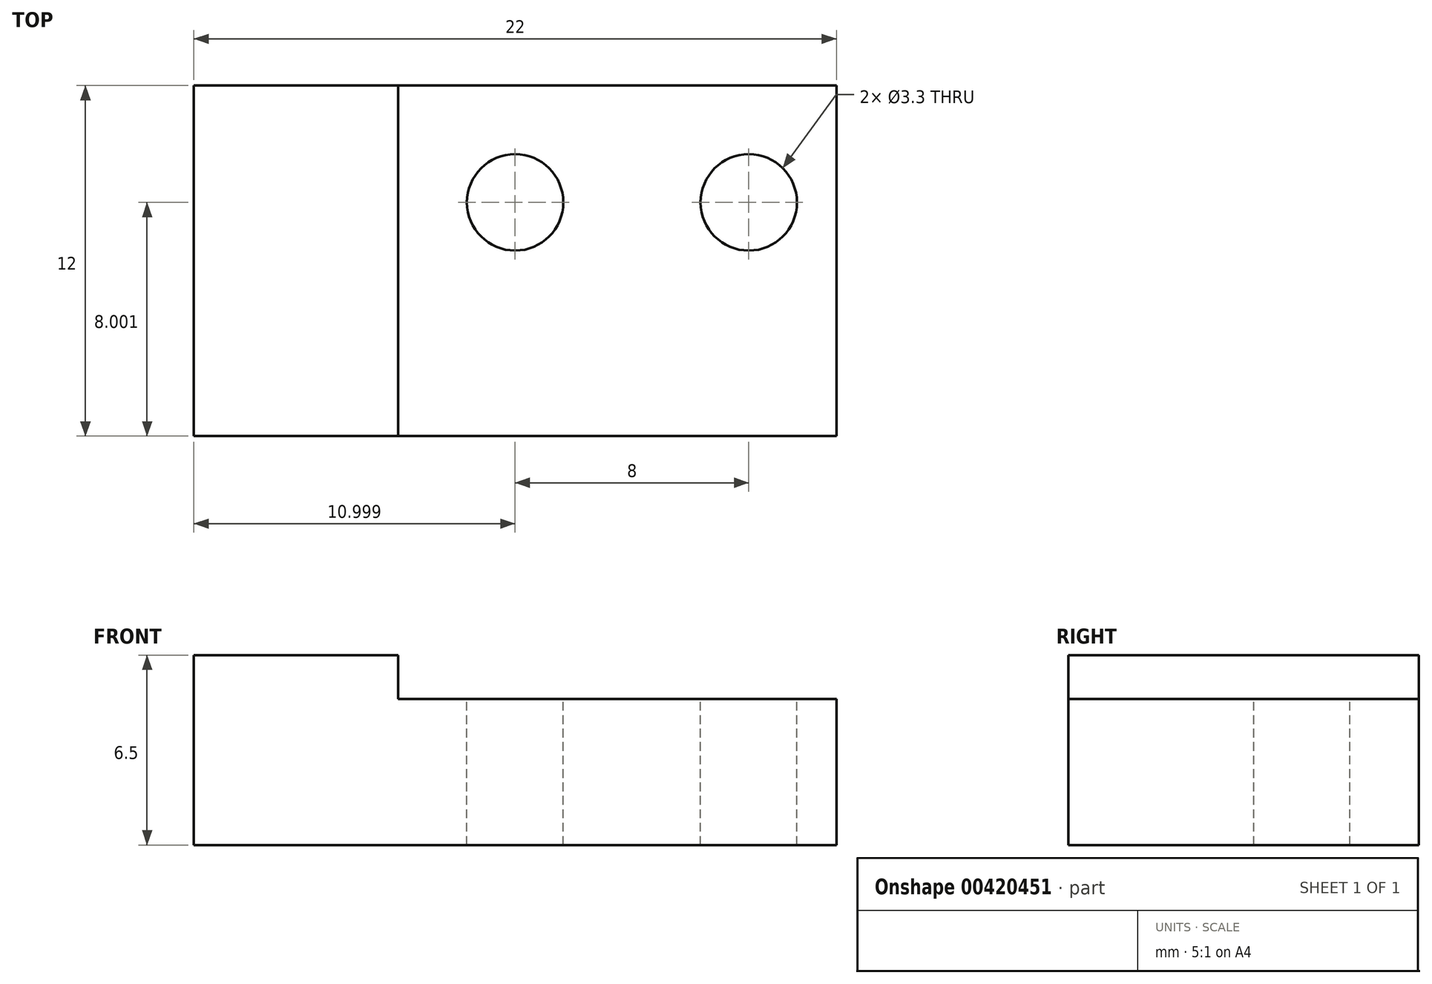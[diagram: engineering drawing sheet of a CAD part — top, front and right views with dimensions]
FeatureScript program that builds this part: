
annotation { "Feature Type Name" : "Feature", "Feature Type Description" : "" }
export const myFeature = defineFeature(function(context is Context, id is Id, definition is map)
    precondition{}
    {
        {
            var Q0;
            Q0=qCreatedBy(makeId("Top.planeOp"),FACE);
            var sketch = newSketch(context, id + "F0", { "sketchPlane" : qUnion([Q0])});
            skLineSegment(sketch, "E0.bottom", {"start": v(-12.24, 8.55) * mm, "end": v(9.76, 8.55) * mm});
            skLineSegment(sketch, "E0.top", {"start": v(-12.24, -3.45) * mm, "end": v(9.76, -3.45) * mm});
            skLineSegment(sketch, "E0.left", {"start": v(-12.24, 8.55) * mm, "end": v(-12.24, -3.45) * mm});
            skLineSegment(sketch, "E0.right", {"start": v(9.76, 8.55) * mm, "end": v(9.76, -3.45) * mm});
            skSolve(sketch);
        }
        {
            var Q0;
            Q0=makeQuery(id+"F0.imprint","IMPRINT",FACE,{"disambiguationData":[TD([[makeQuery(id+"F0.imprint","IMPRINT",EDGE,{"derivedFrom":sQuery(id+"F0.wireOp",EDGE,"E0.bottom")}),-1.0]])]});
            extrude(context, id + "F1", {"entities" : qUnion([Q0]), "depth" : 5 * mm});
        }
        {
            var Q0;
            Q0=makeQuery(id+"F1.opExtrude","CAP_FACE",FACE,{"disambiguationData":[OSD([sQuery(id+"F0.wireOp",EDGE,"E0.bottom"),sQuery(id+"F0.wireOp",EDGE,"E0.top"),sQuery(id+"F0.wireOp",EDGE,"E0.left"),sQuery(id+"F0.wireOp",EDGE,"E0.right")])],"isStart":false});
            var sketch = newSketch(context, id + "F2", { "sketchPlane" : qUnion([Q0])});
            skLineSegment(sketch, "E1.bottom", {"start": v(-12.24, 8.55) * mm, "end": v(-5.24, 8.55) * mm});
            skLineSegment(sketch, "E1.top", {"start": v(-12.24, -3.45) * mm, "end": v(-5.24, -3.45) * mm});
            skLineSegment(sketch, "E1.left", {"start": v(-12.24, 8.55) * mm, "end": v(-12.24, -3.45) * mm});
            skLineSegment(sketch, "E1.right", {"start": v(-5.24, 8.55) * mm, "end": v(-5.24, -3.45) * mm});
            skSolve(sketch);
        }
        {
            var Q0;
            Q0=makeQuery(id+"F2.imprint","IMPRINT",FACE,{"disambiguationData":[TD([[makeQuery(id+"F2.imprint","IMPRINT",EDGE,{"derivedFrom":sQuery(id+"F2.wireOp",EDGE,"E1.bottom")}),-1.0]])]});
            extrude(context, id + "F3", {"entities" : qUnion([Q0]), "operationType" : NewBodyOperationType.ADD, "depth" : 1.5 * mm});
        }
        {
            var Q0;
            Q0=makeQuery(id+"F1.opExtrude","CAP_FACE",FACE,{"disambiguationData":[OSD([sQuery(id+"F0.wireOp",EDGE,"E0.bottom"),sQuery(id+"F0.wireOp",EDGE,"E0.top"),sQuery(id+"F0.wireOp",EDGE,"E0.left"),sQuery(id+"F0.wireOp",EDGE,"E0.right")])],"isStart":false});
            var sketch = newSketch(context, id + "F4", { "sketchPlane" : qUnion([Q0])});
            skPoint(sketch, "E2", {"position": v(-1.24, 4.55) * mm});
            skPoint(sketch, "E3", {"position": v(6.76, 4.55) * mm});
            skSolve(sketch);
        }
        {
            var Q0;
            Q0=sQuery(id+"F4.wireOp",VERTEX,"E2");
            var Q1;
            Q1=sQuery(id+"F4.wireOp",VERTEX,"E3");
            var Q2;
            Q2=makeQuery(id+"F1.opExtrude","SWEPT_BODY",BODY,{"disambiguationData":[OSD([sQuery(id+"F0.wireOp",EDGE,"E0.bottom"),sQuery(id+"F0.wireOp",EDGE,"E0.top"),sQuery(id+"F0.wireOp",EDGE,"E0.left"),sQuery(id+"F0.wireOp",EDGE,"E0.right")])]});
            hole(context, id + "F5", {"style" : HoleStyle.SIMPLE, "endStyle" : HoleEndStyle.THROUGH, "standardTappedOrClearance" : lookupTablePath({ "standard" : "ISO", "fit" : "Normal", "size" : "M3", "type" : "Clearance" }), "standardBlindInLast" : lookupTablePath({ "fit" : "Standard", "standard" : "ISO", "size" : "M3", "type" : "Clearance" }), "holeDiameter" : 3.3 * mm, "isTappedThrough" : true, "tappedDepth" : 17.9 * mm, "tapClearance" : 3, "locations" : qUnion([Q0, Q1]), "scope" : qUnion([Q2])});
        }
    });
